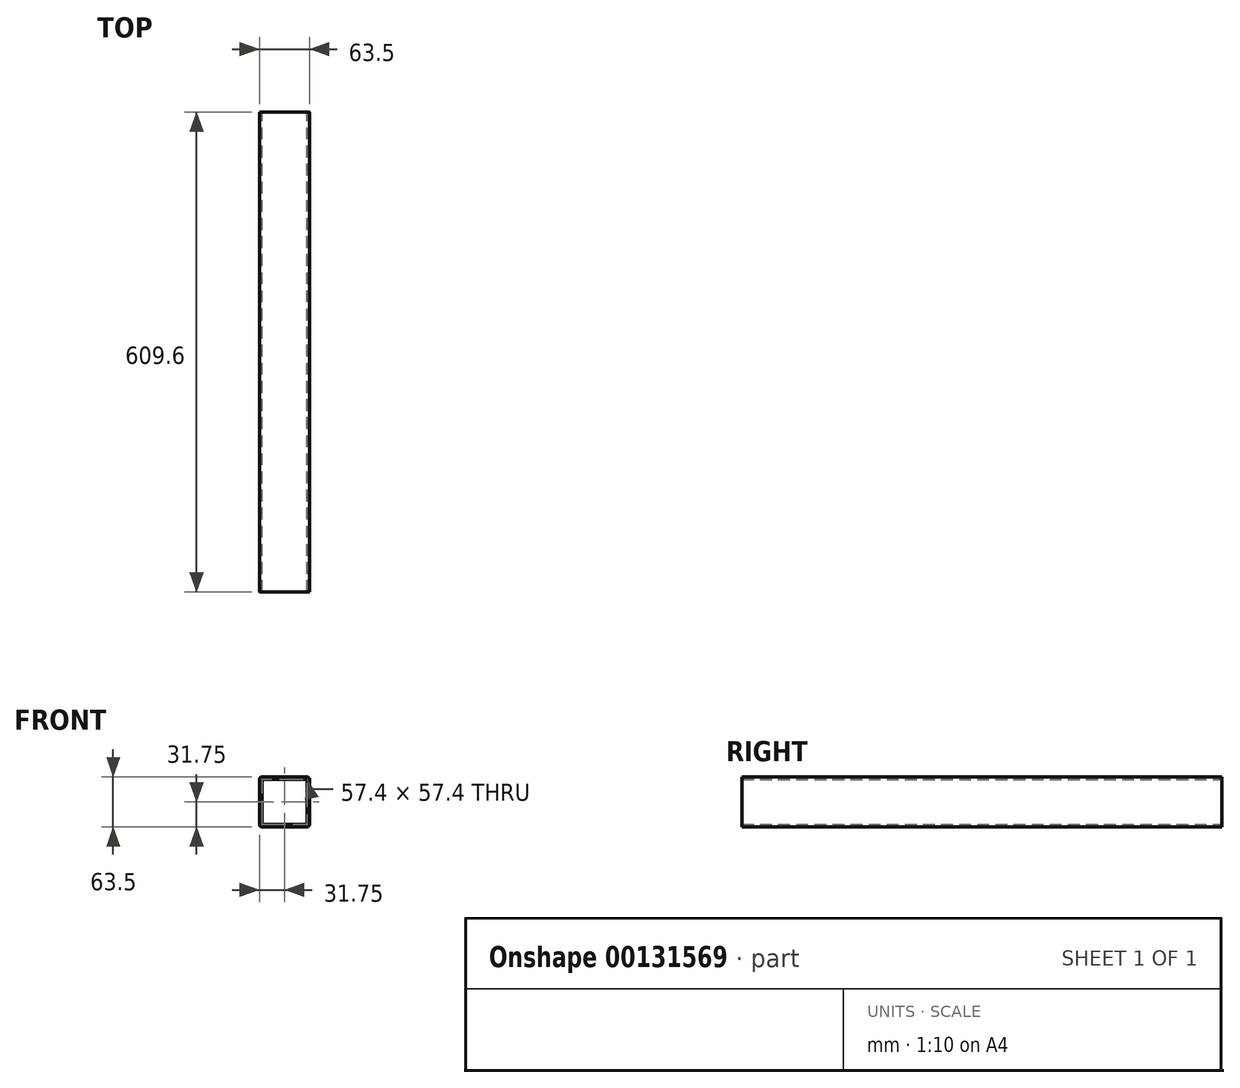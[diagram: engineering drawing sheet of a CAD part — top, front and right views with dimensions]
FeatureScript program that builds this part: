
annotation { "Feature Type Name" : "Feature", "Feature Type Description" : "" }
export const myFeature = defineFeature(function(context is Context, id is Id, definition is map)
    precondition{}
    {
        {
            var Q0;
            Q0=qCreatedBy(makeId("Front.planeOp"),FACE);
            var sketch = newSketch(context, id + "F1", { "sketchPlane" : qUnion([Q0])});
            skLineSegment(sketch, "E0.bottom", {"start": v(28.7, 31.75) * mm, "end": v(-28.7, 31.75) * mm});
            skLineSegment(sketch, "E0.top", {"start": v(28.7, -31.75) * mm, "end": v(-28.7, -31.75) * mm});
            skLineSegment(sketch, "E0.left", {"start": v(31.75, 28.7) * mm, "end": v(31.75, -28.7) * mm});
            skLineSegment(sketch, "E0.right", {"start": v(-31.75, 28.7) * mm, "end": v(-31.75, -28.7) * mm});
            skPoint(sketch, "E0.middle", {"position": v(0, 0) * mm});
            skLineSegment(sketch, "E1.bottom", {"start": v(28.7, 28.7) * mm, "end": v(-28.7, 28.7) * mm});
            skLineSegment(sketch, "E1.top", {"start": v(28.7, -28.7) * mm, "end": v(-28.7, -28.7) * mm});
            skLineSegment(sketch, "E1.left", {"start": v(28.7, 28.7) * mm, "end": v(28.7, -28.7) * mm});
            skLineSegment(sketch, "E1.right", {"start": v(-28.7, 28.7) * mm, "end": v(-28.7, -28.7) * mm});
            skPoint(sketch, "E2.visualSharp", {"position": v(-31.75, 31.75) * mm});
            skArc(sketch, "E2.filletArc", {"start": v(-28.7, 31.75) * mm, "mid": v(-30.86, 30.86) * mm, "end": v(-31.75, 28.7) * mm});
            skPoint(sketch, "E3.visualSharp", {"position": v(-31.75, -31.75) * mm});
            skArc(sketch, "E3.filletArc", {"start": v(-31.75, -28.7) * mm, "mid": v(-30.86, -30.86) * mm, "end": v(-28.7, -31.75) * mm});
            skPoint(sketch, "E4.visualSharp", {"position": v(31.75, -31.75) * mm});
            skArc(sketch, "E4.filletArc", {"start": v(28.7, -31.75) * mm, "mid": v(30.86, -30.86) * mm, "end": v(31.75, -28.7) * mm});
            skPoint(sketch, "E5.visualSharp", {"position": v(31.75, 31.75) * mm});
            skArc(sketch, "E5.filletArc", {"start": v(31.75, 28.7) * mm, "mid": v(30.86, 30.86) * mm, "end": v(28.7, 31.75) * mm});
            skSolve(sketch);
        }
        {
            var Q0;
            Q0=makeQuery(id+"F1.imprint","IMPRINT",FACE,{"disambiguationData":[TD([[makeQuery(id+"F1.imprint","IMPRINT",EDGE,{"derivedFrom":sQuery(id+"F1.wireOp",EDGE,"E0.bottom")}),1.0]])]});
            extrude(context, id + "F0", {"entities" : qUnion([Q0]), "depth" : 609.6 * mm});
        }
    });
